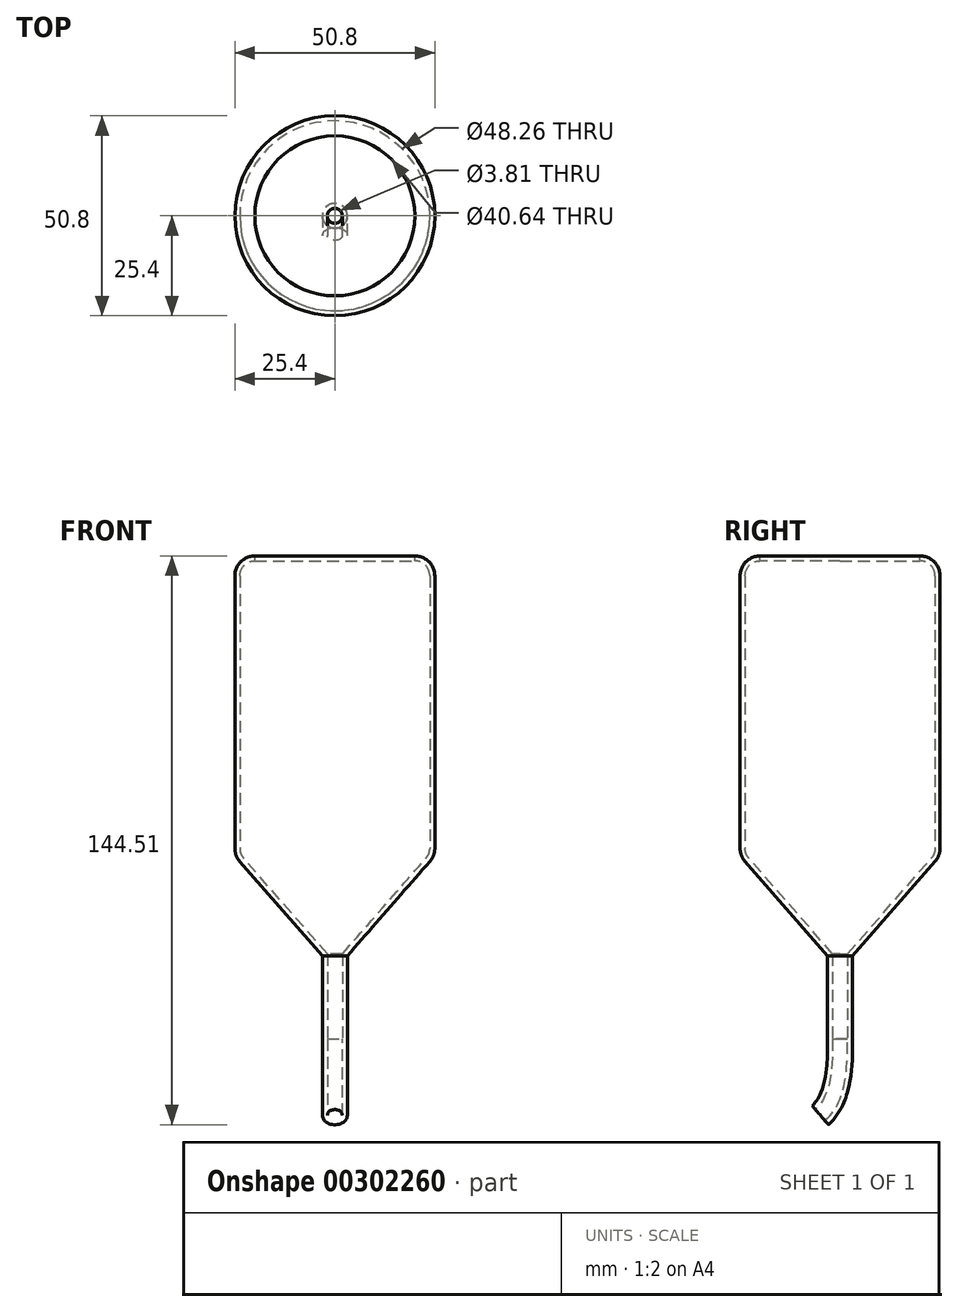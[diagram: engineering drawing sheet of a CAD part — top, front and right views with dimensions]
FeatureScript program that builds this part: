
annotation { "Feature Type Name" : "Feature", "Feature Type Description" : "" }
export const myFeature = defineFeature(function(context is Context, id is Id, definition is map)
    precondition{}
    {
        {
            var Q0;
            Q0=qCreatedBy(makeId("Top.planeOp"),FACE);
            var sketch = newSketch(context, id + "F0", { "sketchPlane" : qUnion([Q0])});
            skCircle(sketch, "E0", {"center": v(0, 0) * mm, "radius": 25.4 * mm});
            skSolve(sketch);
        }
        {
            var Q0;
            Q0 = qSketchRegion(id + "F0", true);
            extrude(context, id + "F1", {"entities" : qUnion([Q0]), "endBound" : BoundingType.SYMMETRIC, "depth" : 76.2 * mm});
        }
        {
            var Q0;
            Q0=makeQuery(id+"F1.opExtrude","CAP_FACE",FACE,{"disambiguationData":[OSD([sQuery(id+"F0.wireOp",EDGE,"E0")])],"isStart":true});
            cPlane(context, id + "F2", {"entities" : qUnion([Q0]), "cplaneType" : CPlaneType.OFFSET, "offset" : 25.4 * mm, "width" : 152.4 * mm, "height" : 152.4 * mm});
        }
        {
            var Q0;
            Q0=qCreatedBy(id+"F2.planeOp",FACE);
            var sketch = newSketch(context, id + "F3", { "sketchPlane" : qUnion([Q0])});
            skCircle(sketch, "E1", {"center": v(0, 0) * mm, "radius": 3.18 * mm});
            skSolve(sketch);
        }
        {
            var Q0;
            Q0=makeQuery(id+"F1.opExtrude","CAP_FACE",FACE,{"disambiguationData":[OSD([sQuery(id+"F0.wireOp",EDGE,"E0")])],"isStart":true});
            var sketch = newSketch(context, id + "F4", { "sketchPlane" : qUnion([Q0])});
            skCircle(sketch, "E2", {"center": v(0, 0) * mm, "radius": 25.4 * mm});
            skSolve(sketch);
        }
        {
            var Q1;
            Q1 = qSketchRegion(id + "F4", true);
            var Q2;
            Q2 = qSketchRegion(id + "F3", true);
            loft(context, id + "F5", {"operationType" : NewBodyOperationType.ADD, "sheetProfilesArray" : [{ "sheetProfileEntities" : qUnion([Q1]) }, { "sheetProfileEntities" : qUnion([Q2]) }]});
        }
        {
            var Q0;
            Q0=qCreatedBy(makeId("Right.planeOp"),FACE);
            var sketch = newSketch(context, id + "F6", { "sketchPlane" : qUnion([Q0])});
            skLineSegment(sketch, "E3", {"start": v(0, -63.81) * mm, "end": v(0, -84.93) * mm});
            skFitSpline(sketch, "E4", {"points": [v(0, -84.93) * mm, v(-5.26, -104.2) * mm], "startDerivative": vector(0, -17.82) * mm, "endDerivative": vector(-15.77, -13.53) * mm});
            skSolve(sketch);
        }
        {
            var Q0;
            Q0=makeQuery(id+"F5.opLoft","CAP_FACE",FACE,{"disambiguationData":[OSD([makeQuery(id+"F3.imprint","IMPRINT",FACE,{"disambiguationData":[TD([[makeQuery(id+"F3.imprint","IMPRINT",EDGE,{"derivedFrom":sQuery(id+"F3.wireOp",EDGE,"E1")}),1.0]])]})])],"isStart":true});
            var sketch = newSketch(context, id + "F7", { "sketchPlane" : qUnion([Q0])});
            skCircle(sketch, "E5", {"center": v(0, 0) * mm, "radius": 3.18 * mm});
            skSolve(sketch);
        }
        {
            var Q0;
            Q0 = qSketchRegion(id + "F7", true);
            var Q1;
            Q1 = qConstructionFilter(qBodyType(qCreatedBy(id + "F6" ,EDGE), BodyType.WIRE), ConstructionObject.NO);
            sweep(context, id + "F8", {"operationType" : NewBodyOperationType.ADD, "profiles" : qUnion([Q0]), "path" : qUnion([Q1])});
        }
        {
            var Q0;
            Q0=makeQuery(id+"F1.opExtrude","CAP_EDGE",EDGE,{"disambiguationData":[OSD([sQuery(id+"F0.wireOp",EDGE,"E0")])],"isStart":false});
            var Q1;
            Q1=makeQuery(id+"F5.boolean.opBoolean","MERGE",EDGE,{"derivedFrom":[makeQuery(id+"F1.opExtrude","CAP_EDGE",EDGE,{"disambiguationData":[OSD([sQuery(id+"F0.wireOp",EDGE,"E0")])],"isStart":true}),makeQuery(id+"F5.opLoft","MID_CAP_EDGE",EDGE,{"disambiguationData":[OSD([sQuery(id+"F4.wireOp",EDGE,"E2")])],"capPos":0.0})]});
            fillet(context, id + "F9", {"entities" : qUnion([Q0, Q1]), "radius" : 5.08 * mm, "tangentPropagation" : true, "allowEdgeOverflow" : false});
        }
        {
            var Q0;
            Q0=makeQuery(id+"F8.opSweep","CAP_FACE",FACE,{"disambiguationData":[OSD([sQuery(id+"F6.wireOp",VERTEX,"E4.end"),sQuery(id+"F7.wireOp",EDGE,"E5")])],"isStart":false});
            shell(context, id + "F10", {"entities" : qUnion([Q0]), "thickness" : 1.27 * mm});
        }
        {
            var Q0;
            Q0=makeQuery(id+"F1.opExtrude","CAP_FACE",FACE,{"disambiguationData":[OSD([sQuery(id+"F0.wireOp",EDGE,"E0")])],"isStart":false});
            var sketch = newSketch(context, id + "F11", { "sketchPlane" : qUnion([Q0])});
            skCircle(sketch, "E6", {"center": v(0, 0) * mm, "radius": 20.32 * mm});
            skSolve(sketch);
        }
        {
            var Q0;
            Q0 = qSketchRegion(id + "F11", true);
            extrude(context, id + "F12", {"entities" : qUnion([Q0]), "operationType" : NewBodyOperationType.REMOVE, "endBound" : BoundingType.UP_TO_NEXT, "oppositeDirection" : true, "depth" : 25.4 * mm});
        }
    });
